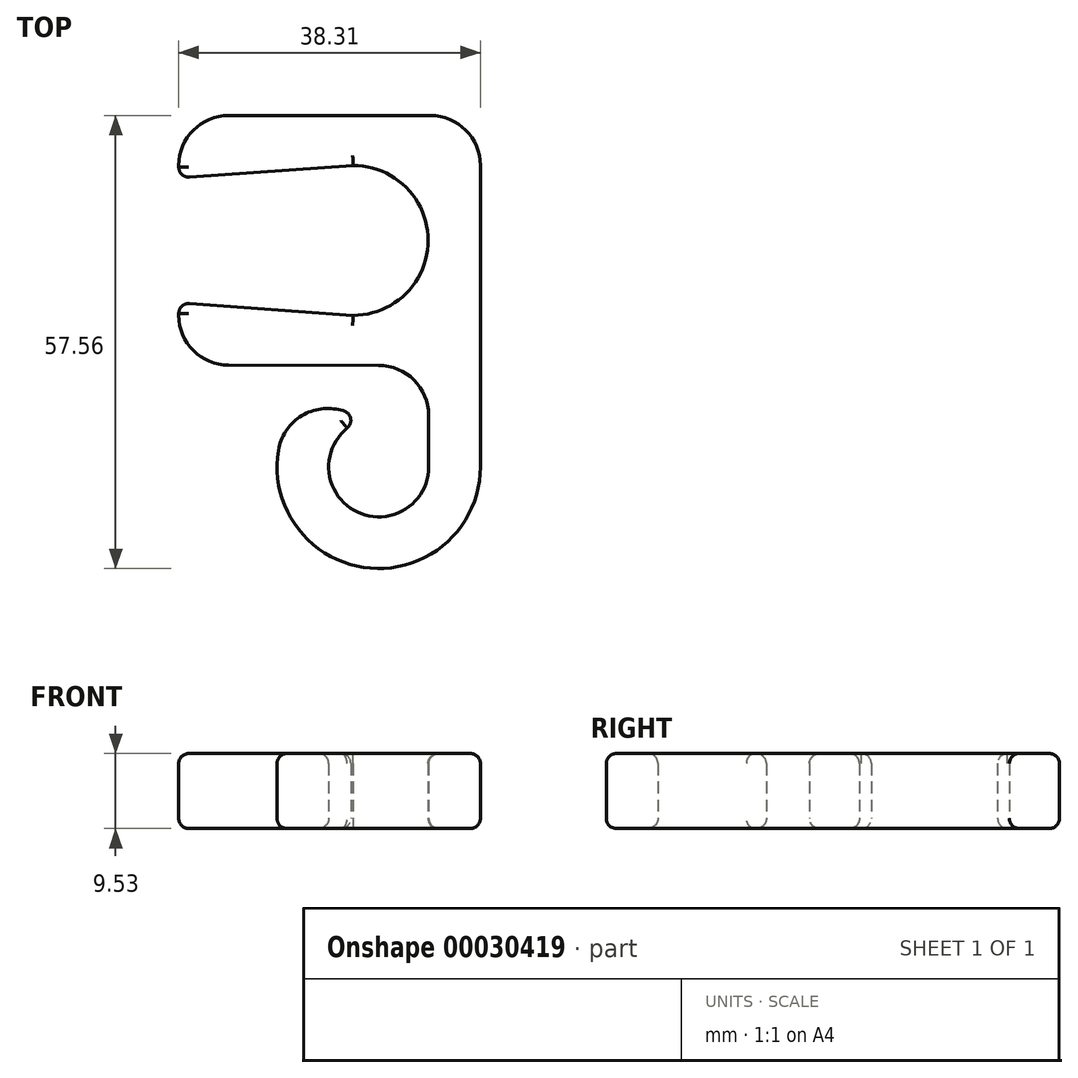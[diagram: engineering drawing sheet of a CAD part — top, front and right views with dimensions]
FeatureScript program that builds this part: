
annotation { "Feature Type Name" : "Feature", "Feature Type Description" : "" }
export const myFeature = defineFeature(function(context is Context, id is Id, definition is map)
    precondition{}
    {
        {
            var Q0;
            Q0=qCreatedBy(makeId("Top.planeOp"),FACE);
            var sketch = newSketch(context, id + "F0", { "sketchPlane" : qUnion([Q0])});
            skArc(sketch, "E0", {"start": v(-0.75, 6.3) * mm, "mid": v(-4.2, -4.75) * mm, "end": v(6.35, 0.02) * mm});
            skArc(sketch, "E1", {"start": v(-12.74, 2.1) * mm, "mid": v(-1.06, -12.87) * mm, "end": v(12.91, 0) * mm});
            skArc(sketch, "E2", {"start": v(-3.26, 19.25) * mm, "mid": v(6.27, 28.77) * mm, "end": v(-3.25, 38.3) * mm});
            skLineSegment(sketch, "E3", {"start": v(-25.4, 19.26) * mm, "end": v(-25.4, 19.26) * mm});
            skLineSegment(sketch, "E4", {"start": v(12.91, 0) * mm, "end": v(12.91, 38.3) * mm});
            skPoint(sketch, "E5.start.orphan", {"position": v(0, 37.72) * mm});
            skLineSegment(sketch, "E6", {"start": v(-25.4, 38.3) * mm, "end": v(-25.4, 38.3) * mm});
            skLineSegment(sketch, "E7", {"start": v(-19.05, 44.65) * mm, "end": v(6.56, 44.65) * mm});
            skLineSegment(sketch, "E8", {"start": v(-5.1, 7.27) * mm, "end": v(-0.75, 6.3) * mm});
            skPoint(sketch, "E9.orphan", {"position": v(6.27, 28.77) * mm});
            skPoint(sketch, "E10.visualSharp", {"position": v(12.91, 44.65) * mm});
            skArc(sketch, "E10.filletArc", {"start": v(12.91, 38.3) * mm, "mid": v(11.05, 42.79) * mm, "end": v(6.56, 44.65) * mm});
            skPoint(sketch, "E11.visualSharp", {"position": v(-25.4, 44.65) * mm});
            skArc(sketch, "E11.filletArc", {"start": v(-19.05, 44.65) * mm, "mid": v(-23.54, 42.79) * mm, "end": v(-25.4, 38.3) * mm});
            skPoint(sketch, "E12.visualSharp", {"position": v(-25.4, 12.91) * mm});
            skArc(sketch, "E12.filletArc", {"start": v(-25.4, 19.26) * mm, "mid": v(-23.54, 14.77) * mm, "end": v(-19.05, 12.91) * mm});
            skPoint(sketch, "E13.visualSharp", {"position": v(-9.87, 8.33) * mm});
            skArc(sketch, "E13.filletArc", {"start": v(-5.1, 7.27) * mm, "mid": v(-10.03, 6.33) * mm, "end": v(-12.74, 2.1) * mm});
            skLineSegment(sketch, "E14", {"start": v(-25.4, 19.26) * mm, "end": v(-25.4, 20.85) * mm});
            skLineSegment(sketch, "E15", {"start": v(-25.4, 38.3) * mm, "end": v(-25.4, 36.7) * mm});
            skLineSegment(sketch, "E16", {"start": v(-25.4, 36.7) * mm, "end": v(-3.25, 38.3) * mm});
            skLineSegment(sketch, "E17", {"start": v(-25.4, 20.85) * mm, "end": v(-3.26, 19.25) * mm});
            skLineSegment(sketch, "E18", {"start": v(-19.05, 12.91) * mm, "end": v(-0.01, 12.9) * mm});
            skLineSegment(sketch, "E19", {"start": v(6.35, 0.02) * mm, "end": v(6.33, 6.56) * mm});
            skPoint(sketch, "E20.visualSharp", {"position": v(6.31, 12.89) * mm});
            skArc(sketch, "E20.filletArc", {"start": v(6.33, 6.56) * mm, "mid": v(4.47, 11.04) * mm, "end": v(-0.01, 12.9) * mm});
            skSolve(sketch);
        }
        {
            var Q0;
            Q0=makeQuery(id+"F0.imprint","IMPRINT",FACE,{"disambiguationData":[TD([[makeQuery(id+"F0.imprint","IMPRINT",EDGE,{"derivedFrom":sQuery(id+"F0.wireOp",EDGE,"E0")}),-1.0]])]});
            extrude(context, id + "F1", {"entities" : qUnion([Q0]), "depth" : 9.52 * mm});
        }
        {
            var Q0;
            Q0=makeQuery(id+"F1.opExtrude","CAP_EDGE",EDGE,{"disambiguationData":[OSD([sQuery(id+"F0.wireOp",EDGE,"E0")])],"isStart":false});
            var Q1;
            Q1=makeQuery(id+"F1.opExtrude","CAP_EDGE",EDGE,{"disambiguationData":[OSD([sQuery(id+"F0.wireOp",EDGE,"E0")])],"isStart":true});
            fillet(context, id + "F2", {"entities" : qUnion([Q0, Q1]), "radius" : 1.27 * mm, "tangentPropagation" : true, "allowEdgeOverflow" : false});
        }
        {
            var Q0;
            Q0=makeQuery(id+"F1.opExtrude","SWEPT_EDGE",EDGE,{"disambiguationData":[OSD([sQuery(id+"F0.wireOp",EDGE,"E0"),sQuery(id+"F0.wireOp",EDGE,"E8")])]});
            fillet(context, id + "F3", {"entities" : qUnion([Q0]), "radius" : 1.27 * mm, "tangentPropagation" : true, "allowEdgeOverflow" : false});
        }
        {
            var Q0;
            Q0=makeQuery(id+"F1.opExtrude","CAP_EDGE",EDGE,{"disambiguationData":[OSD([sQuery(id+"F0.wireOp",EDGE,"E16")])],"isStart":true});
            var Q1;
            Q1=makeQuery(id+"F1.opExtrude","CAP_EDGE",EDGE,{"disambiguationData":[OSD([sQuery(id+"F0.wireOp",EDGE,"E17")])],"isStart":true});
            fillet(context, id + "F4", {"entities" : qUnion([Q0, Q1]), "radius" : 1.27 * mm, "tangentPropagation" : true, "allowEdgeOverflow" : false});
        }
    });
